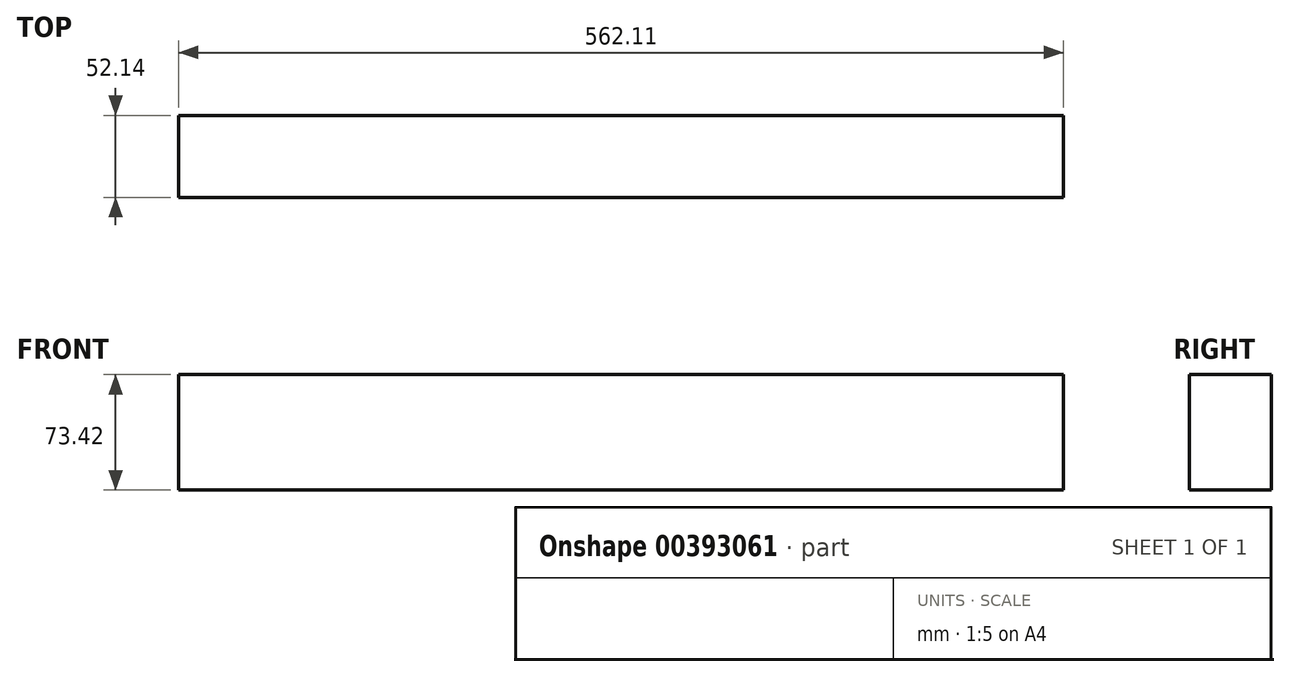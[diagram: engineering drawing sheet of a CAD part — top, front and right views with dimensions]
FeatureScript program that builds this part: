
annotation { "Feature Type Name" : "Feature", "Feature Type Description" : "" }
export const myFeature = defineFeature(function(context is Context, id is Id, definition is map)
    precondition{}
    {
        {
            var Q0;
            Q0=qCreatedBy(makeId("Right.planeOp"),FACE);
            var sketch = newSketch(context, id + "F0", { "sketchPlane" : qUnion([Q0])});
            skLineSegment(sketch, "E0.bottom", {"start": v(19.8, -16.44) * mm, "end": v(-32.33, -16.44) * mm});
            skLineSegment(sketch, "E0.top", {"start": v(19.8, 56.98) * mm, "end": v(-32.33, 56.98) * mm});
            skLineSegment(sketch, "E0.left", {"start": v(19.8, -16.44) * mm, "end": v(19.8, 56.98) * mm});
            skLineSegment(sketch, "E0.right", {"start": v(-32.33, -16.44) * mm, "end": v(-32.33, 56.98) * mm});
            skSolve(sketch);
        }
        {
            var Q0;
            Q0 = qSketchRegion(id + "F0", true);
            extrude(context, id + "F1", {"entities" : qUnion([Q0]), "depth" : 562.1 * mm});
        }
    });
